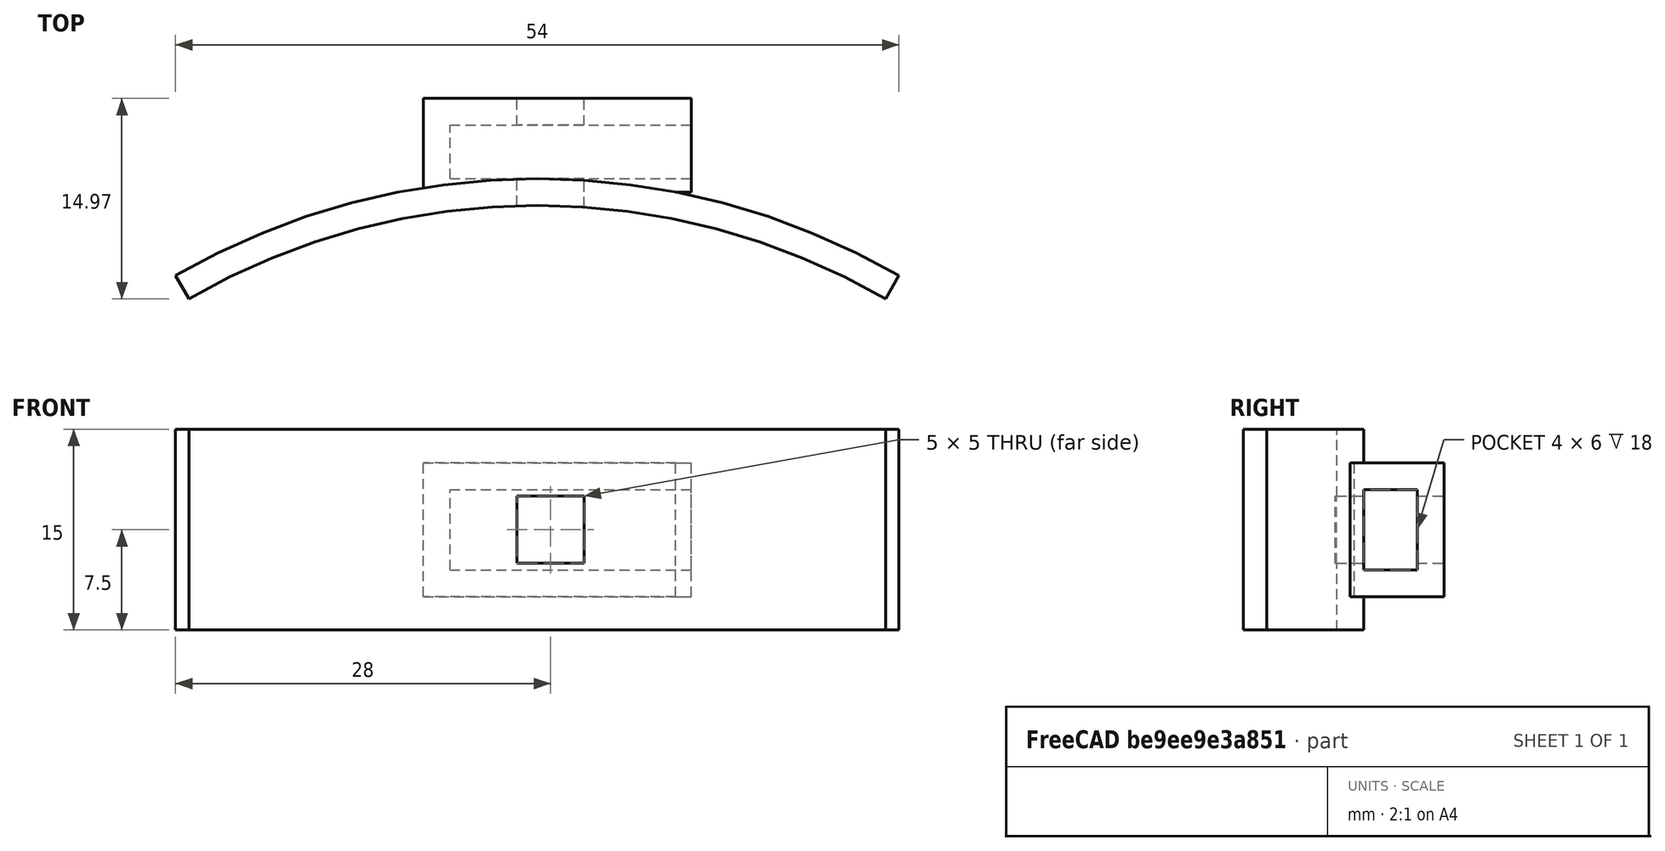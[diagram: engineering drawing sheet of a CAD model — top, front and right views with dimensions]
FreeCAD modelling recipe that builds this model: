
FCSTD DOCUMENT  (FreeCAD 0.16R4924 (Git))
Label: solenoid_bay_v3
License: All rights reserved
LicenseURL: http://en.wikipedia.org/wiki/All_rights_reserved
objects: Part::Cut×3, Part::Box×3, Part::Cylinder×2, Part::MultiFuse×2
note: 10 computed .brp shape members not serialized (recipe doc carries the construction recipe); baked Part::Feature solids carry a one-line shape summary decoded from their .brp

FEATURE [Part::Cylinder] Cylinder  label="bottle_wall"
  Angle = 60
  Height = 15
  Placement = pos=(8.5,-7,0) rot=(0,0,1;1.0472rad)
  Radius = 54
FEATURE [Part::Cylinder] Cylinder001  label="bottle_wall001"
  Angle = 60
  Height = 15
  Placement = pos=(8.5,-7,0) rot=(0,0,1;1.0472rad)
  Radius = 52
FEATURE [Part::Cut] Cut
  Base = -> Cylinder
  Placement = pos=(0,-2,0) rot=(0,0,1;0rad)
  Tool = -> Cylinder001
FEATURE [Part::Box] Box  label="pin_opening"
  Height = 5
  Length = 5
  Placement = pos=(7,42,5) rot=(0,0,1;0rad)
  Width = 20
FEATURE [Part::Box] Box001  label="latch"
  Height = 10
  Length = 20
  Placement = pos=(0,44,2.5) rot=(0,0,1;0rad)
  Width = 7
FEATURE [Part::MultiFuse] Fusion
  Shapes = -> [Cut,Box001]
FEATURE [Part::MultiFuse] Fusion001
  Shapes = -> [Fusion,Box001]
FEATURE [Part::Cut] Cut001
  Base = -> Fusion001
  Tool = -> Box
FEATURE [Part::Box] Box002  label="slot"
  Height = 6
  Length = 20
  Placement = pos=(2,45,4.5) rot=(0,0,1;0rad)
  Width = 4
FEATURE [Part::Cut] Cut002
  Base = -> Cut001
  Tool = -> Box002
